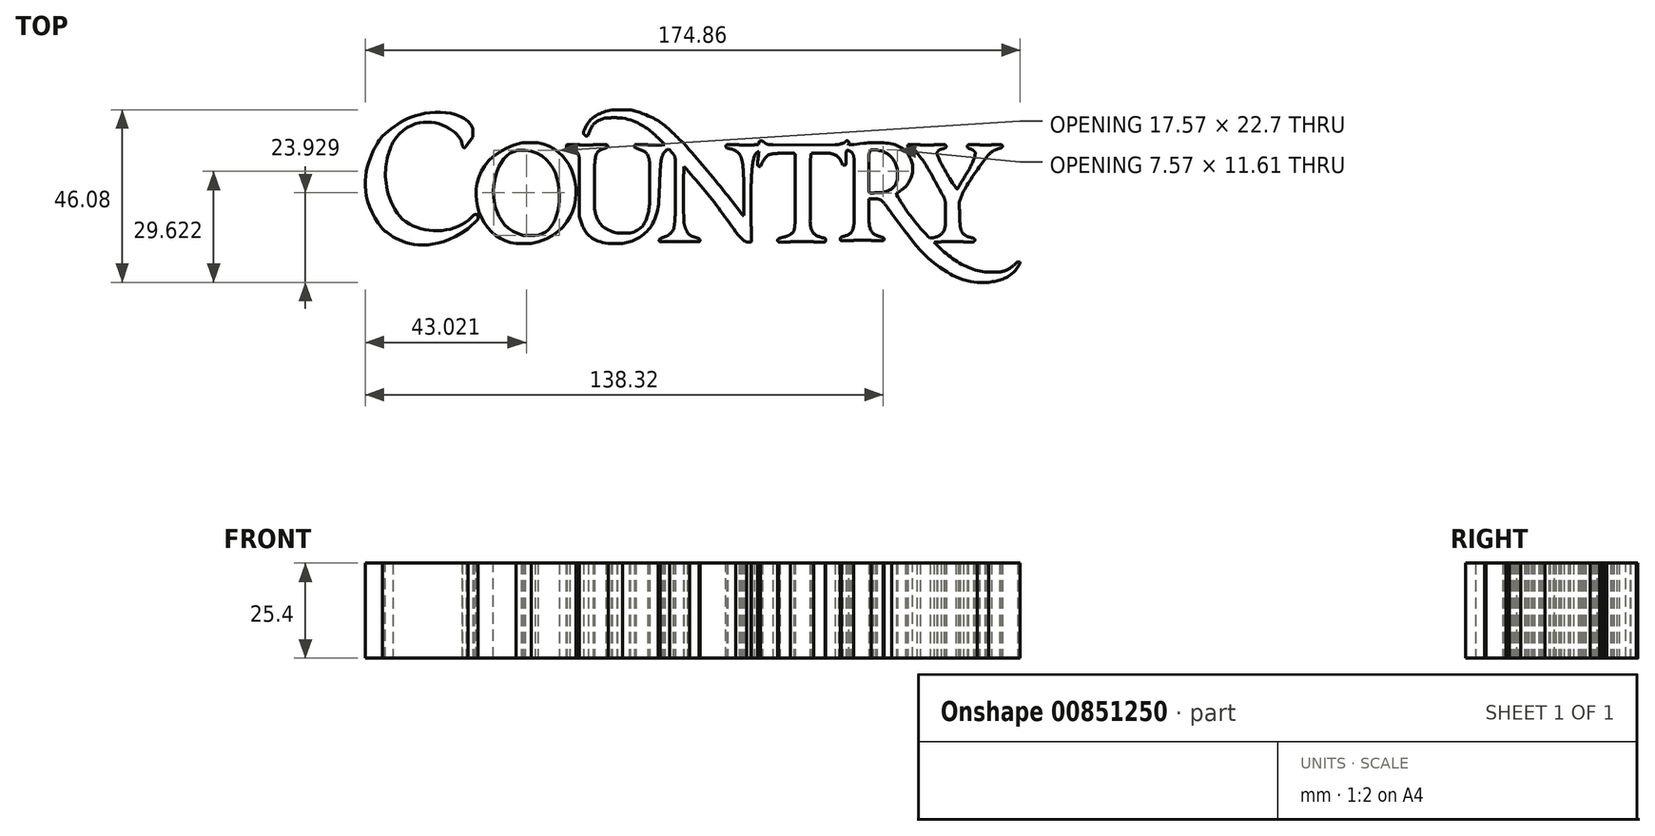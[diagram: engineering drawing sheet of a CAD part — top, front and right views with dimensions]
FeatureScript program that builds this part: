
annotation { "Feature Type Name" : "Feature", "Feature Type Description" : "" }
export const myFeature = defineFeature(function(context is Context, id is Id, definition is map)
    precondition{}
    {
        {
            var Q0;
            Q0=qCreatedBy(makeId("Top.planeOp"),FACE);
            var sketch = newSketch(context, id + "F0", { "sketchPlane" : qUnion([Q0])});
            skFitSpline(sketch, "E0", {"points": [v(35.4, 49.52) * mm, v(16.81, 50.27) * mm], "startDerivative": vector(0.37, 12.53) * mm, "endDerivative": vector(-20.2, -31.14) * mm});
            skFitSpline(sketch, "E1", {"points": [v(16.81, 50.27) * mm, v(16.81, 33.45) * mm], "startDerivative": vector(-2.43, -5.61) * mm, "endDerivative": vector(11.65, -23.52) * mm});
            skFitSpline(sketch, "E2", {"points": [v(16.81, 33.45) * mm, v(38.58, 30.97) * mm], "startDerivative": vector(11.04, -25.12) * mm, "endDerivative": vector(15.53, 18.9) * mm});
            skFitSpline(sketch, "E3", {"points": [v(35.4, 49.52) * mm, v(36.47, 49.27) * mm], "startDerivative": vector(1.66, -3.64) * mm, "endDerivative": vector(0.9, 0.95) * mm});
            skLineSegment(sketch, "E4", {"start": v(36.47, 49.27) * mm, "end": v(38.26, 51.69) * mm});
            skFitSpline(sketch, "E5", {"points": [v(38.26, 51.69) * mm, v(38.26, 53.99) * mm], "startDerivative": vector(0, 2.3) * mm, "endDerivative": vector(0, 2.3) * mm});
            skFitSpline(sketch, "E6", {"points": [v(38.26, 53.99) * mm, v(23.7, 57.64) * mm, v(14.1, 51.93) * mm], "startDerivative": vector(-11.12, 26.02) * mm, "endDerivative": vector(-17.74, -14.88) * mm});
            skFitSpline(sketch, "E7", {"points": [v(14.1, 51.93) * mm, v(14.1, 27.24) * mm], "startDerivative": vector(-5.04, -5.16) * mm, "endDerivative": vector(28.36, -33.37) * mm});
            skFitSpline(sketch, "E8", {"points": [v(14.1, 27.24) * mm, v(36.9, 27.24) * mm], "startDerivative": vector(1.85, -2.26) * mm, "endDerivative": vector(39.15, 28.31) * mm});
            skLineSegment(sketch, "E9", {"start": v(36.9, 27.24) * mm, "end": v(39.6, 29.74) * mm});
            skLineSegment(sketch, "E10", {"start": v(39.6, 29.74) * mm, "end": v(39.6, 30.8) * mm});
            skLineSegment(sketch, "E11", {"start": v(38.58, 30.97) * mm, "end": v(39.43, 30.97) * mm});
            skLineSegment(sketch, "E12", {"start": v(39.43, 30.97) * mm, "end": v(39.6, 30.8) * mm});
            skFitSpline(sketch, "E13", {"points": [v(51.22, 48.17) * mm, v(51.72, 25.47) * mm], "startDerivative": vector(-26, 1.12) * mm, "endDerivative": vector(35.77, -7.77) * mm});
            skLineSegment(sketch, "E14", {"start": v(51.72, 25.47) * mm, "end": v(54.79, 25.47) * mm});
            skLineSegment(sketch, "E15", {"start": v(51.22, 48.17) * mm, "end": v(52.14, 48.17) * mm});
            skFitSpline(sketch, "E16", {"points": [v(52.14, 48.17) * mm, v(61.13, 33.26) * mm, v(54.79, 25.47) * mm], "startDerivative": vector(42.6, -3.97) * mm, "endDerivative": vector(-25, -0.76) * mm});
            skFitSpline(sketch, "E17", {"points": [v(49.82, 23.27) * mm, v(51.38, 50.14) * mm], "startDerivative": vector(-36.1, 3) * mm, "endDerivative": vector(55.93, 12.72) * mm});
            skLineSegment(sketch, "E18", {"start": v(49.82, 23.27) * mm, "end": v(53.76, 23.27) * mm});
            skLineSegment(sketch, "E19", {"start": v(51.38, 50.14) * mm, "end": v(55.64, 50.14) * mm});
            skFitSpline(sketch, "E20", {"points": [v(55.64, 50.14) * mm, v(53.76, 23.27) * mm], "startDerivative": vector(36.31, -4.68) * mm, "endDerivative": vector(-52.22, -10.47) * mm});
            skLineSegment(sketch, "E21", {"start": v(66.78, 49.57) * mm, "end": v(70.36, 49.57) * mm});
            skLineSegment(sketch, "E22", {"start": v(85, 49.57) * mm, "end": v(88.8, 49.57) * mm});
            skLineSegment(sketch, "E23", {"start": v(70.36, 49.57) * mm, "end": v(70.36, 49.71) * mm});
            skLineSegment(sketch, "E24", {"start": v(70.36, 49.71) * mm, "end": v(74, 49.71) * mm});
            skLineSegment(sketch, "E25", {"start": v(66.78, 49.57) * mm, "end": v(66.78, 49.71) * mm});
            skLineSegment(sketch, "E26", {"start": v(66.78, 49.71) * mm, "end": v(63.37, 49.71) * mm});
            skFitSpline(sketch, "E27", {"points": [v(63.37, 49.71) * mm, v(64.08, 48.7) * mm], "startDerivative": vector(-1.53, -2.11) * mm, "endDerivative": vector(2.16, -0.35) * mm});
            skFitSpline(sketch, "E28", {"points": [v(64.08, 48.7) * mm, v(66.56, 46.62) * mm, v(66.7, 45.12) * mm], "startDerivative": vector(10.09, -2.85) * mm, "endDerivative": vector(-0.3, -3.52) * mm});
            skLineSegment(sketch, "E29", {"start": v(66.7, 45.12) * mm, "end": v(66.7, 30.52) * mm});
            skFitSpline(sketch, "E30", {"points": [v(66.7, 30.52) * mm, v(74.4, 23.22) * mm], "startDerivative": vector(2.7, -8.8) * mm, "endDerivative": vector(19, -3) * mm});
            skLineSegment(sketch, "E31", {"start": v(74.4, 23.22) * mm, "end": v(78.2, 23.22) * mm});
            skFitSpline(sketch, "E32", {"points": [v(78.2, 23.22) * mm, v(87.75, 33.2) * mm], "startDerivative": vector(11.51, 2.34) * mm, "endDerivative": vector(3.28, 21.51) * mm});
            skFitSpline(sketch, "E33", {"points": [v(88.38, 44.39) * mm, v(87.75, 33.2) * mm], "startDerivative": vector(-0.75, -9.45) * mm, "endDerivative": vector(-1.12, -11.5) * mm});
            skFitSpline(sketch, "E34", {"points": [v(90.5, 48.5) * mm, v(88.38, 44.39) * mm], "startDerivative": vector(-3.28, -1.12) * mm, "endDerivative": vector(-0.66, -7.86) * mm});
            skLineSegment(sketch, "E35", {"start": v(88.8, 49.57) * mm, "end": v(88.8, 49.71) * mm});
            skLineSegment(sketch, "E36", {"start": v(88.8, 49.71) * mm, "end": v(89.51, 49.71) * mm});
            skLineSegment(sketch, "E37", {"start": v(85, 49.57) * mm, "end": v(85, 49.71) * mm});
            skLineSegment(sketch, "E38", {"start": v(85, 49.71) * mm, "end": v(81.56, 49.71) * mm});
            skFitSpline(sketch, "E39", {"points": [v(81.56, 49.71) * mm, v(81.72, 48.76) * mm], "startDerivative": vector(-1.26, -1.45) * mm, "endDerivative": vector(1, -0.66) * mm});
            skFitSpline(sketch, "E40", {"points": [v(81.72, 48.76) * mm, v(84.5, 47.4) * mm, v(85.34, 45.46) * mm, v(85.49, 44.42) * mm], "startDerivative": vector(7.4, -2.3) * mm, "endDerivative": vector(0.54, -3.4) * mm});
            skLineSegment(sketch, "E41", {"start": v(85.49, 44.42) * mm, "end": v(85.49, 34.19) * mm});
            skFitSpline(sketch, "E42", {"points": [v(85.49, 34.19) * mm, v(80.22, 26.05) * mm], "startDerivative": vector(-1.17, -10.57) * mm, "endDerivative": vector(-12.8, -2.78) * mm});
            skLineSegment(sketch, "E43", {"start": v(80.22, 26.05) * mm, "end": v(76.85, 26.05) * mm});
            skFitSpline(sketch, "E44", {"points": [v(70.67, 32.85) * mm, v(76.85, 26.05) * mm], "startDerivative": vector(1.31, -5.14) * mm, "endDerivative": vector(17.22, -3.66) * mm});
            skLineSegment(sketch, "E45", {"start": v(70.67, 32.85) * mm, "end": v(70.67, 43.78) * mm});
            skFitSpline(sketch, "E46", {"points": [v(70.67, 43.78) * mm, v(73.7, 48.74) * mm], "startDerivative": vector(1.16, 8.1) * mm, "endDerivative": vector(9.13, 1.89) * mm});
            skFitSpline(sketch, "E47", {"points": [v(74, 49.71) * mm, v(73.7, 48.74) * mm], "startDerivative": vector(0.96, -0.92) * mm, "endDerivative": vector(-1.98, -0.88) * mm});
            skLineSegment(sketch, "E48", {"start": v(90.5, 48.5) * mm, "end": v(91.72, 47.22) * mm});
            skFitSpline(sketch, "E49", {"points": [v(91.72, 47.22) * mm, v(92.34, 44.94) * mm], "startDerivative": vector(1.39, -1.75) * mm, "endDerivative": vector(0.13, -3.4) * mm});
            skLineSegment(sketch, "E50", {"start": v(92.34, 44.94) * mm, "end": v(92.34, 32.57) * mm});
            skFitSpline(sketch, "E51", {"points": [v(92.34, 32.57) * mm, v(91.84, 27.12) * mm], "startDerivative": vector(-0.46, -9.87) * mm, "endDerivative": vector(-0.95, -4.55) * mm});
            skFitSpline(sketch, "E52", {"points": [v(91.84, 27.12) * mm, v(89, 24.91) * mm], "startDerivative": vector(-2.58, -4.23) * mm, "endDerivative": vector(-4.45, -1.18) * mm});
            skFitSpline(sketch, "E53", {"points": [v(89, 24.91) * mm, v(88.22, 23.71) * mm], "startDerivative": vector(-2.09, -0.83) * mm, "endDerivative": vector(1.89, -1.61) * mm});
            skLineSegment(sketch, "E54", {"start": v(88.22, 23.71) * mm, "end": v(90.75, 23.71) * mm});
            skLineSegment(sketch, "E55", {"start": v(90.75, 23.71) * mm, "end": v(90.75, 23.83) * mm});
            skLineSegment(sketch, "E56", {"start": v(90.75, 23.83) * mm, "end": v(96.08, 23.83) * mm});
            skLineSegment(sketch, "E57", {"start": v(96.08, 23.83) * mm, "end": v(96.08, 23.71) * mm});
            skLineSegment(sketch, "E58", {"start": v(96.08, 23.71) * mm, "end": v(98.61, 23.71) * mm});
            skFitSpline(sketch, "E59", {"points": [v(98.61, 23.71) * mm, v(98.61, 24.6) * mm], "startDerivative": vector(1.1, 0.96) * mm, "endDerivative": vector(-1.18, 1.22) * mm});
            skFitSpline(sketch, "E60", {"points": [v(98.61, 24.6) * mm, v(95.44, 26.46) * mm], "startDerivative": vector(-3.86, 1.65) * mm, "endDerivative": vector(-2.22, 4.33) * mm});
            skFitSpline(sketch, "E61", {"points": [v(95.44, 26.46) * mm, v(94.54, 29.77) * mm], "startDerivative": vector(-1.57, 2.4) * mm, "endDerivative": vector(-0.16, 4.17) * mm});
            skLineSegment(sketch, "E62", {"start": v(94.54, 29.77) * mm, "end": v(94.42, 32.53) * mm});
            skLineSegment(sketch, "E63", {"start": v(94.42, 32.53) * mm, "end": v(94.42, 41.82) * mm});
            skLineSegment(sketch, "E64", {"start": v(94.42, 41.82) * mm, "end": v(94.54, 41.82) * mm});
            skLineSegment(sketch, "E65", {"start": v(94.54, 41.82) * mm, "end": v(94.54, 43.88) * mm});
            skFitSpline(sketch, "E66", {"points": [v(94.54, 43.88) * mm, v(108.5, 26.3) * mm], "startDerivative": vector(15.6, -16.67) * mm, "endDerivative": vector(13.53, -19.21) * mm});
            skFitSpline(sketch, "E67", {"points": [v(108.5, 26.3) * mm, v(111.41, 23.61) * mm], "startDerivative": vector(2.23, -2.59) * mm, "endDerivative": vector(5.04, -2.36) * mm});
            skLineSegment(sketch, "E68", {"start": v(111.41, 23.61) * mm, "end": v(112.5, 23.61) * mm});
            skLineSegment(sketch, "E69", {"start": v(112.5, 23.61) * mm, "end": v(112.69, 23.71) * mm});
            skLineSegment(sketch, "E70", {"start": v(112.69, 23.71) * mm, "end": v(112.69, 27.78) * mm});
            skLineSegment(sketch, "E71", {"start": v(112.69, 27.78) * mm, "end": v(112.55, 27.78) * mm});
            skLineSegment(sketch, "E72", {"start": v(112.55, 27.78) * mm, "end": v(112.55, 39.2) * mm});
            skLineSegment(sketch, "E73", {"start": v(112.55, 39.2) * mm, "end": v(112.69, 39.2) * mm});
            skFitSpline(sketch, "E74", {"points": [v(112.69, 39.2) * mm, v(114.62, 47.85) * mm], "startDerivative": vector(-0.38, 14.87) * mm, "endDerivative": vector(4.17, 1.11) * mm});
            skLineSegment(sketch, "E75", {"start": v(110.54, 40.86) * mm, "end": v(110.54, 30.76) * mm});
            skLineSegment(sketch, "E76", {"start": v(110.54, 30.76) * mm, "end": v(110.28, 30.76) * mm});
            skLineSegment(sketch, "E77", {"start": v(110.28, 30.76) * mm, "end": v(110.28, 30.93) * mm});
            skFitSpline(sketch, "E78", {"points": [v(110.54, 40.86) * mm, v(109.8, 46.5) * mm], "startDerivative": vector(-0.4, 5.94) * mm, "endDerivative": vector(-1.99, 4.96) * mm});
            skFitSpline(sketch, "E79", {"points": [v(109.8, 46.5) * mm, v(106.27, 48.7) * mm], "startDerivative": vector(-1.67, 3.66) * mm, "endDerivative": vector(-5.1, 0.7) * mm});
            skFitSpline(sketch, "E80", {"points": [v(106.27, 48.7) * mm, v(106.06, 49.71) * mm], "startDerivative": vector(-1.2, 0.32) * mm, "endDerivative": vector(1.47, 1.28) * mm});
            skLineSegment(sketch, "E81", {"start": v(106.06, 49.71) * mm, "end": v(109.27, 49.71) * mm});
            skLineSegment(sketch, "E82", {"start": v(109.27, 49.71) * mm, "end": v(109.27, 49.59) * mm});
            skLineSegment(sketch, "E83", {"start": v(109.27, 49.59) * mm, "end": v(113.41, 49.59) * mm});
            skLineSegment(sketch, "E84", {"start": v(113.41, 49.59) * mm, "end": v(113.41, 49.71) * mm});
            skLineSegment(sketch, "E85", {"start": v(113.41, 49.71) * mm, "end": v(114.58, 49.71) * mm});
            skFitSpline(sketch, "E86", {"points": [v(114.58, 49.71) * mm, v(114.8, 50.67) * mm], "startDerivative": vector(0.04, 1.5) * mm, "endDerivative": vector(0.37, 0.82) * mm});
            skLineSegment(sketch, "E87", {"start": v(114.8, 50.67) * mm, "end": v(115.57, 50.67) * mm});
            skFitSpline(sketch, "E88", {"points": [v(115.57, 50.67) * mm, v(118.38, 49.62) * mm], "startDerivative": vector(1.45, -1.64) * mm, "endDerivative": vector(4.91, 0.05) * mm});
            skLineSegment(sketch, "E89", {"start": v(118.38, 49.62) * mm, "end": v(118.38, 49.55) * mm});
            skLineSegment(sketch, "E90", {"start": v(118.38, 49.55) * mm, "end": v(135.03, 49.62) * mm});
            skLineSegment(sketch, "E91", {"start": v(135.03, 49.62) * mm, "end": v(135.03, 49.7) * mm});
            skLineSegment(sketch, "E92", {"start": v(135.03, 49.7) * mm, "end": v(135.9, 49.7) * mm});
            skFitSpline(sketch, "E93", {"points": [v(94.43, 50.17) * mm, v(110.28, 30.93) * mm], "startDerivative": vector(17.31, -19.68) * mm, "endDerivative": vector(14.9, -19.4) * mm});
            skFitSpline(sketch, "E94", {"points": [v(94.43, 50.17) * mm, v(81.81, 58.56) * mm], "startDerivative": vector(-12.75, 11.35) * mm, "endDerivative": vector(-22.1, 6.9) * mm});
            skFitSpline(sketch, "E95", {"points": [v(81.81, 58.56) * mm, v(79.98, 58.97) * mm], "startDerivative": vector(-3.59, 1.05) * mm, "endDerivative": vector(-1.9, 0.1) * mm});
            skLineSegment(sketch, "E96", {"start": v(79.98, 58.97) * mm, "end": v(75.43, 58.97) * mm});
            skFitSpline(sketch, "E97", {"points": [v(75.43, 58.97) * mm, v(70.83, 57.23) * mm, v(68.94, 55.38) * mm, v(67.85, 53.35) * mm], "startDerivative": vector(-14.63, -3.27) * mm, "endDerivative": vector(-3.27, -7.37) * mm});
            skLineSegment(sketch, "E98", {"start": v(67.85, 53.35) * mm, "end": v(67.85, 52.52) * mm});
            skFitSpline(sketch, "E99", {"points": [v(67.85, 52.52) * mm, v(69.13, 52.32) * mm], "startDerivative": vector(0.73, -0.68) * mm, "endDerivative": vector(1.6, 2.25) * mm});
            skFitSpline(sketch, "E100", {"points": [v(73.9, 56.85) * mm, v(69.13, 52.32) * mm], "startDerivative": vector(-9.13, -2.63) * mm, "endDerivative": vector(-2.45, -8.55) * mm});
            skLineSegment(sketch, "E101", {"start": v(73.9, 56.85) * mm, "end": v(75.2, 56.85) * mm});
            skLineSegment(sketch, "E102", {"start": v(75.2, 56.85) * mm, "end": v(75.2, 56.98) * mm});
            skLineSegment(sketch, "E103", {"start": v(75.2, 56.98) * mm, "end": v(76.74, 56.98) * mm});
            skLineSegment(sketch, "E104", {"start": v(76.74, 56.98) * mm, "end": v(76.74, 56.85) * mm});
            skLineSegment(sketch, "E105", {"start": v(76.74, 56.85) * mm, "end": v(78.18, 56.85) * mm});
            skFitSpline(sketch, "E106", {"points": [v(78.18, 56.85) * mm, v(89.51, 49.71) * mm], "startDerivative": vector(18.02, -4.05) * mm, "endDerivative": vector(8.49, -8.07) * mm});
            skFitSpline(sketch, "E107", {"points": [v(135.9, 49.7) * mm, v(137.85, 50.62) * mm, v(138.43, 50.65) * mm], "startDerivative": vector(8.67, 2.15) * mm, "endDerivative": vector(2.65, -0.92) * mm});
            skFitSpline(sketch, "E108", {"points": [v(138.43, 50.65) * mm, v(138.62, 50.43) * mm, v(138.66, 49.89) * mm], "startDerivative": vector(0.53, -0.49) * mm, "endDerivative": vector(-0.04, -1.01) * mm});
            skLineSegment(sketch, "E109", {"start": v(138.66, 49.89) * mm, "end": v(138.53, 49.85) * mm});
            skLineSegment(sketch, "E110", {"start": v(138.53, 49.85) * mm, "end": v(138.53, 49.6) * mm});
            skLineSegment(sketch, "E111", {"start": v(138.53, 49.6) * mm, "end": v(138.59, 49.6) * mm});
            skLineSegment(sketch, "E112", {"start": v(138.59, 49.6) * mm, "end": v(138.66, 49.72) * mm});
            skLineSegment(sketch, "E113", {"start": v(138.66, 49.72) * mm, "end": v(140.06, 49.72) * mm});
            skFitSpline(sketch, "E114", {"points": [v(140.06, 49.72) * mm, v(144.58, 50.17) * mm, v(148.1, 50.14) * mm, v(151.5, 49.47) * mm, v(153.84, 48.08) * mm], "startDerivative": vector(40.03, 4.88) * mm, "endDerivative": vector(9.83, -6.75) * mm});
            skFitSpline(sketch, "E115", {"points": [v(153.84, 48.08) * mm, v(153.86, 38.46) * mm], "startDerivative": vector(5.86, -7.74) * mm, "endDerivative": vector(-9.07, -11.51) * mm});
            skFitSpline(sketch, "E116", {"points": [v(153.86, 38.46) * mm, v(151.4, 36.7) * mm], "startDerivative": vector(-2.47, -2.07) * mm, "endDerivative": vector(-2.27, -1.4) * mm});
            skLineSegment(sketch, "E117", {"start": v(151.4, 36.7) * mm, "end": v(151.4, 36.28) * mm});
            skFitSpline(sketch, "E118", {"points": [v(151.4, 36.28) * mm, v(160.33, 24.7) * mm], "startDerivative": vector(7.88, -13.13) * mm, "endDerivative": vector(12.28, -11.88) * mm});
            skLineSegment(sketch, "E119", {"start": v(144.05, 47.15) * mm, "end": v(144.05, 37.05) * mm});
            skFitSpline(sketch, "E120", {"points": [v(144.05, 47.15) * mm, v(144.7, 48.32) * mm], "startDerivative": vector(0.31, 1.87) * mm, "endDerivative": vector(1.12, 0.58) * mm});
            skLineSegment(sketch, "E121", {"start": v(144.7, 48.32) * mm, "end": v(145.73, 48.32) * mm});
            skFitSpline(sketch, "E122", {"points": [v(145.73, 48.32) * mm, v(151.61, 43.03) * mm], "startDerivative": vector(10.02, -1.37) * mm, "endDerivative": vector(2.62, -9.79) * mm});
            skLineSegment(sketch, "E123", {"start": v(151.61, 43.03) * mm, "end": v(151.61, 40.33) * mm});
            skFitSpline(sketch, "E124", {"points": [v(151.61, 40.33) * mm, v(148.08, 37) * mm], "startDerivative": vector(-1.52, -6.16) * mm, "endDerivative": vector(-5.33, -1.45) * mm});
            skFitSpline(sketch, "E125", {"points": [v(148.08, 37) * mm, v(145.15, 36.77) * mm], "startDerivative": vector(-3.03, -0.66) * mm, "endDerivative": vector(-2.93, -0.23) * mm});
            skFitSpline(sketch, "E126", {"points": [v(144.05, 37.05) * mm, v(145.15, 36.77) * mm], "startDerivative": vector(0.58, -0.73) * mm, "endDerivative": vector(2.04, 0.5) * mm});
            skFitSpline(sketch, "E127", {"points": [v(114.62, 47.85) * mm, v(114.32, 44.22) * mm, v(114.62, 43.85) * mm, v(115.08, 43.86) * mm], "startDerivative": vector(-1.05, -10.58) * mm, "endDerivative": vector(2.31, 0.33) * mm});
            skFitSpline(sketch, "E128", {"points": [v(115.08, 43.86) * mm, v(116.93, 46.73) * mm, v(119.62, 47.3) * mm], "startDerivative": vector(2.94, 6.54) * mm, "endDerivative": vector(6.16, 0.22) * mm});
            skLineSegment(sketch, "E129", {"start": v(119.62, 47.3) * mm, "end": v(119.62, 47.4) * mm});
            skLineSegment(sketch, "E130", {"start": v(119.62, 47.4) * mm, "end": v(123.95, 47.4) * mm});
            skFitSpline(sketch, "E131", {"points": [v(123.95, 47.4) * mm, v(124.33, 46.66) * mm], "startDerivative": vector(0.9, -0.3) * mm, "endDerivative": vector(0.08, -0.81) * mm});
            skLineSegment(sketch, "E132", {"start": v(124.33, 46.66) * mm, "end": v(124.33, 29.52) * mm});
            skFitSpline(sketch, "E133", {"points": [v(124.33, 29.52) * mm, v(124, 26.71) * mm], "startDerivative": vector(-0.26, -3.16) * mm, "endDerivative": vector(-0.62, -2.51) * mm});
            skFitSpline(sketch, "E134", {"points": [v(124, 26.71) * mm, v(120.3, 24.71) * mm], "startDerivative": vector(-2.5, -4.53) * mm, "endDerivative": vector(-3.62, -1.28) * mm});
            skFitSpline(sketch, "E135", {"points": [v(119.66, 23.93) * mm, v(119.86, 23.7) * mm], "startDerivative": vector(0.1, -0.38) * mm, "endDerivative": vector(0.27, -0.16) * mm});
            skLineSegment(sketch, "E136", {"start": v(119.86, 23.7) * mm, "end": v(123.1, 23.7) * mm});
            skLineSegment(sketch, "E137", {"start": v(123.1, 23.7) * mm, "end": v(123.1, 23.82) * mm});
            skLineSegment(sketch, "E138", {"start": v(123.1, 23.82) * mm, "end": v(129.2, 23.82) * mm});
            skLineSegment(sketch, "E139", {"start": v(129.2, 23.82) * mm, "end": v(129.2, 23.7) * mm});
            skLineSegment(sketch, "E140", {"start": v(129.2, 23.7) * mm, "end": v(132.25, 23.7) * mm});
            skFitSpline(sketch, "E141", {"points": [v(132.25, 23.7) * mm, v(132.25, 24.67) * mm], "startDerivative": vector(1.05, 0.7) * mm, "endDerivative": vector(-0.9, 0.8) * mm});
            skFitSpline(sketch, "E142", {"points": [v(120.3, 24.71) * mm, v(119.66, 23.93) * mm], "startDerivative": vector(-1.71, -0.53) * mm, "endDerivative": vector(0.03, -1.68) * mm});
            skFitSpline(sketch, "E143", {"points": [v(132.25, 24.67) * mm, v(128.32, 29.7) * mm], "startDerivative": vector(-8, 1.8) * mm, "endDerivative": vector(0.33, 11.08) * mm});
            skLineSegment(sketch, "E144", {"start": v(128.32, 29.7) * mm, "end": v(128.32, 43.44) * mm});
            skFitSpline(sketch, "E145", {"points": [v(128.32, 43.44) * mm, v(128.67, 47.33) * mm], "startDerivative": vector(0.1, 6.4) * mm, "endDerivative": vector(0.55, 0.87) * mm});
            skLineSegment(sketch, "E146", {"start": v(132.43, 47.4) * mm, "end": v(128.83, 47.4) * mm});
            skLineSegment(sketch, "E147", {"start": v(128.83, 47.4) * mm, "end": v(128.67, 47.33) * mm});
            skFitSpline(sketch, "E148", {"points": [v(132.43, 47.4) * mm, v(137, 44.25) * mm], "startDerivative": vector(6.82, -0.04) * mm, "endDerivative": vector(2.64, -7.59) * mm});
            skFitSpline(sketch, "E149", {"points": [v(137, 44.25) * mm, v(137.72, 44.25) * mm, v(137.88, 45.96) * mm, v(137.95, 47.46) * mm, v(138.16, 48.12) * mm, v(138.7, 48.07) * mm, v(139.19, 47.8) * mm], "startDerivative": vector(6.6, -0.87) * mm, "endDerivative": vector(3.4, -2.29) * mm});
            skFitSpline(sketch, "E150", {"points": [v(139.19, 47.8) * mm, v(140.12, 45.04) * mm], "startDerivative": vector(2.85, -1.99) * mm, "endDerivative": vector(0.5, -2.48) * mm});
            skLineSegment(sketch, "E151", {"start": v(140.1, 45.04) * mm, "end": v(140.12, 45.04) * mm});
            skLineSegment(sketch, "E152", {"start": v(140.1, 45.04) * mm, "end": v(140.12, 29.84) * mm});
            skFitSpline(sketch, "E153", {"points": [v(140.12, 29.84) * mm, v(136.8, 25.03) * mm], "startDerivative": vector(-0.83, -11.38) * mm, "endDerivative": vector(-7.63, -1.97) * mm});
            skFitSpline(sketch, "E154", {"points": [v(136.8, 25.03) * mm, v(136.58, 24) * mm], "startDerivative": vector(-2.43, -1.14) * mm, "endDerivative": vector(0.43, -0.2) * mm});
            skLineSegment(sketch, "E155", {"start": v(136.58, 24) * mm, "end": v(139.96, 24) * mm});
            skLineSegment(sketch, "E156", {"start": v(139.96, 24) * mm, "end": v(139.96, 24.14) * mm});
            skLineSegment(sketch, "E157", {"start": v(139.96, 24.14) * mm, "end": v(144.6, 24.14) * mm});
            skLineSegment(sketch, "E158", {"start": v(144.6, 24.14) * mm, "end": v(144.6, 24) * mm});
            skLineSegment(sketch, "E159", {"start": v(144.6, 24) * mm, "end": v(147.77, 24) * mm});
            skFitSpline(sketch, "E160", {"points": [v(147.77, 24) * mm, v(147.87, 24.86) * mm], "startDerivative": vector(0.73, 0.4) * mm, "endDerivative": vector(-1.26, 1.24) * mm});
            skFitSpline(sketch, "E161", {"points": [v(144.04, 29.02) * mm, v(147.87, 24.86) * mm], "startDerivative": vector(0.87, -9.2) * mm, "endDerivative": vector(7.75, -1.92) * mm});
            skLineSegment(sketch, "E162", {"start": v(144.04, 29.02) * mm, "end": v(144.04, 35.18) * mm});
            skLineSegment(sketch, "E163", {"start": v(144.04, 35.18) * mm, "end": v(146.12, 35.18) * mm});
            skFitSpline(sketch, "E164", {"points": [v(146.12, 35.18) * mm, v(147.2, 34.85) * mm, v(150.05, 31.3) * mm], "startDerivative": vector(3.07, -0.27) * mm, "endDerivative": vector(4.61, -6.75) * mm});
            skFitSpline(sketch, "E165", {"points": [v(150.05, 31.3) * mm, v(156.49, 23) * mm, v(161.12, 18.32) * mm, v(165.04, 15.54) * mm, v(167.07, 14.44) * mm, v(170.38, 13.34) * mm, v(172.9, 12.9) * mm], "startDerivative": vector(26.64, -35.75) * mm, "endDerivative": vector(19.29, -2.6) * mm});
            skLineSegment(sketch, "E166", {"start": v(172.9, 12.9) * mm, "end": v(176.03, 12.9) * mm});
            skFitSpline(sketch, "E167", {"points": [v(176.03, 12.9) * mm, v(184.37, 17.96) * mm], "startDerivative": vector(12.1, 1.84) * mm, "endDerivative": vector(4.96, 10.1) * mm});
            skLineSegment(sketch, "E168", {"start": v(184.37, 17.96) * mm, "end": v(184.37, 18.36) * mm});
            skLineSegment(sketch, "E169", {"start": v(184.37, 18.36) * mm, "end": v(183.71, 18.36) * mm});
            skFitSpline(sketch, "E170", {"points": [v(183.71, 18.36) * mm, v(178.87, 15.65) * mm], "startDerivative": vector(-4.6, -4.26) * mm, "endDerivative": vector(-6.74, -0.75) * mm});
            skLineSegment(sketch, "E171", {"start": v(178.87, 15.65) * mm, "end": v(174.93, 15.65) * mm});
            skFitSpline(sketch, "E172", {"points": [v(161.38, 23.68) * mm, v(174.93, 15.65) * mm], "startDerivative": vector(12.07, -13.13) * mm, "endDerivative": vector(14.3, -1.83) * mm});
            skLineSegment(sketch, "E173", {"start": v(161.38, 23.68) * mm, "end": v(163.32, 23.68) * mm});
            skLineSegment(sketch, "E174", {"start": v(163.32, 23.68) * mm, "end": v(163.32, 23.81) * mm});
            skLineSegment(sketch, "E175", {"start": v(163.32, 23.81) * mm, "end": v(169.3, 23.81) * mm});
            skLineSegment(sketch, "E176", {"start": v(169.3, 23.81) * mm, "end": v(169.3, 23.68) * mm});
            skLineSegment(sketch, "E177", {"start": v(169.3, 23.68) * mm, "end": v(171.9, 23.68) * mm});
            skFitSpline(sketch, "E178", {"points": [v(171.9, 23.68) * mm, v(171.9, 24.68) * mm], "startDerivative": vector(1.53, 0.7) * mm, "endDerivative": vector(-1.56, 0.58) * mm});
            skFitSpline(sketch, "E179", {"points": [v(168.44, 27.65) * mm, v(171.9, 24.68) * mm], "startDerivative": vector(0.7, -5.97) * mm, "endDerivative": vector(5.74, -1.5) * mm});
            skFitSpline(sketch, "E180", {"points": [v(168.44, 27.65) * mm, v(168.25, 29.92) * mm, v(168.18, 34.2) * mm], "startDerivative": vector(-0.52, 4.95) * mm, "endDerivative": vector(-0.01, 8) * mm});
            skFitSpline(sketch, "E181", {"points": [v(168.18, 34.2) * mm, v(175.34, 46.23) * mm], "startDerivative": vector(2.31, 10.95) * mm, "endDerivative": vector(7.91, 11.34) * mm});
            skFitSpline(sketch, "E182", {"points": [v(175.34, 46.23) * mm, v(179.31, 48.76) * mm], "startDerivative": vector(4.65, 5.7) * mm, "endDerivative": vector(3.59, 0.65) * mm});
            skFitSpline(sketch, "E183", {"points": [v(179.31, 48.76) * mm, v(179.38, 49.7) * mm], "startDerivative": vector(1.04, 0.53) * mm, "endDerivative": vector(-1.55, 0.92) * mm});
            skLineSegment(sketch, "E184", {"start": v(179.38, 49.7) * mm, "end": v(176.8, 49.7) * mm});
            skLineSegment(sketch, "E185", {"start": v(176.8, 49.7) * mm, "end": v(176.8, 49.57) * mm});
            skLineSegment(sketch, "E186", {"start": v(176.8, 49.57) * mm, "end": v(173.62, 49.57) * mm});
            skLineSegment(sketch, "E187", {"start": v(173.62, 49.57) * mm, "end": v(173.62, 49.7) * mm});
            skLineSegment(sketch, "E188", {"start": v(173.62, 49.7) * mm, "end": v(170.6, 49.7) * mm});
            skFitSpline(sketch, "E189", {"points": [v(170.6, 49.7) * mm, v(170.6, 48.68) * mm], "startDerivative": vector(-1.14, -0.85) * mm, "endDerivative": vector(1.24, -0.97) * mm});
            skFitSpline(sketch, "E190", {"points": [v(170.6, 48.68) * mm, v(172.46, 47.36) * mm], "startDerivative": vector(2.55, -0.65) * mm, "endDerivative": vector(0.7, -2.35) * mm});
            skFitSpline(sketch, "E191", {"points": [v(172.46, 47.36) * mm, v(167.9, 38.24) * mm], "startDerivative": vector(-1.82, -10.06) * mm, "endDerivative": vector(-4.55, -9.1) * mm});
            skFitSpline(sketch, "E192", {"points": [v(167.9, 38.24) * mm, v(167.2, 38.24) * mm], "startDerivative": vector(-1.02, -1.9) * mm, "endDerivative": vector(-0.79, 1.19) * mm});
            skFitSpline(sketch, "E193", {"points": [v(167.2, 38.24) * mm, v(162.27, 47) * mm, v(162.24, 47.66) * mm], "startDerivative": vector(-9.43, 13.77) * mm, "endDerivative": vector(0.47, 2.46) * mm});
            skFitSpline(sketch, "E194", {"points": [v(162.24, 47.66) * mm, v(164.21, 48.7) * mm], "startDerivative": vector(1.37, 2.2) * mm, "endDerivative": vector(2.26, 0.62) * mm});
            skFitSpline(sketch, "E195", {"points": [v(164.21, 48.7) * mm, v(164.3, 49.7) * mm], "startDerivative": vector(1.78, 0.72) * mm, "endDerivative": vector(-1.34, 0.86) * mm});
            skLineSegment(sketch, "E196", {"start": v(161.4, 49.7) * mm, "end": v(164.3, 49.7) * mm});
            skLineSegment(sketch, "E197", {"start": v(161.4, 49.7) * mm, "end": v(161.4, 49.57) * mm});
            skLineSegment(sketch, "E198", {"start": v(161.4, 49.57) * mm, "end": v(157.67, 49.57) * mm});
            skLineSegment(sketch, "E199", {"start": v(157.67, 49.57) * mm, "end": v(157.67, 49.7) * mm});
            skLineSegment(sketch, "E200", {"start": v(157.67, 49.7) * mm, "end": v(154.42, 49.7) * mm});
            skLineSegment(sketch, "E201", {"start": v(154.42, 49.7) * mm, "end": v(154.42, 49.05) * mm});
            skFitSpline(sketch, "E202", {"points": [v(154.42, 49.05) * mm, v(156.87, 47.5) * mm], "startDerivative": vector(1.92, -1.44) * mm, "endDerivative": vector(1.99, -3.26) * mm});
            skFitSpline(sketch, "E203", {"points": [v(156.87, 47.5) * mm, v(164.06, 35.58) * mm], "startDerivative": vector(9.12, -10.81) * mm, "endDerivative": vector(7.1, -11.9) * mm});
            skFitSpline(sketch, "E204", {"points": [v(164.06, 35.58) * mm, v(164.4, 34.32) * mm, v(164.47, 32.82) * mm], "startDerivative": vector(0.84, -2.54) * mm, "endDerivative": vector(-0.03, -2.98) * mm});
            skLineSegment(sketch, "E205", {"start": v(164.47, 32.82) * mm, "end": v(164.47, 28.7) * mm});
            skFitSpline(sketch, "E206", {"points": [v(164.47, 28.7) * mm, v(160.33, 24.7) * mm], "startDerivative": vector(-0.2, -7.9) * mm, "endDerivative": vector(-8, -0.8) * mm});
            skSolve(sketch);
        }
        {
            var Q0;
            Q0=makeQuery(id+"F0.imprint","IMPRINT",FACE,{"disambiguationData":[TD([[makeQuery(id+"F0.imprint","IMPRINT",EDGE,{"derivedFrom":sQuery(id+"F0.wireOp",EDGE,"E0")}),-1.0]])]});
            var Q1;
            Q1=makeQuery(id+"F0.imprint","IMPRINT",FACE,{"disambiguationData":[TD([[makeQuery(id+"F0.imprint","IMPRINT",EDGE,{"derivedFrom":sQuery(id+"F0.wireOp",EDGE,"E13")}),-1.0]])]});
            var Q2;
            Q2=makeQuery(id+"F0.imprint","IMPRINT",FACE,{"disambiguationData":[TD([[makeQuery(id+"F0.imprint","IMPRINT",EDGE,{"derivedFrom":sQuery(id+"F0.wireOp",EDGE,"E21")}),-1.0]])]});
            extrude(context, id + "F1", {"entities" : qUnion([Q0, Q1, Q2]), "depth" : 25.4 * mm, "offsetDistance" : 25.4 * mm});
        }
    });
